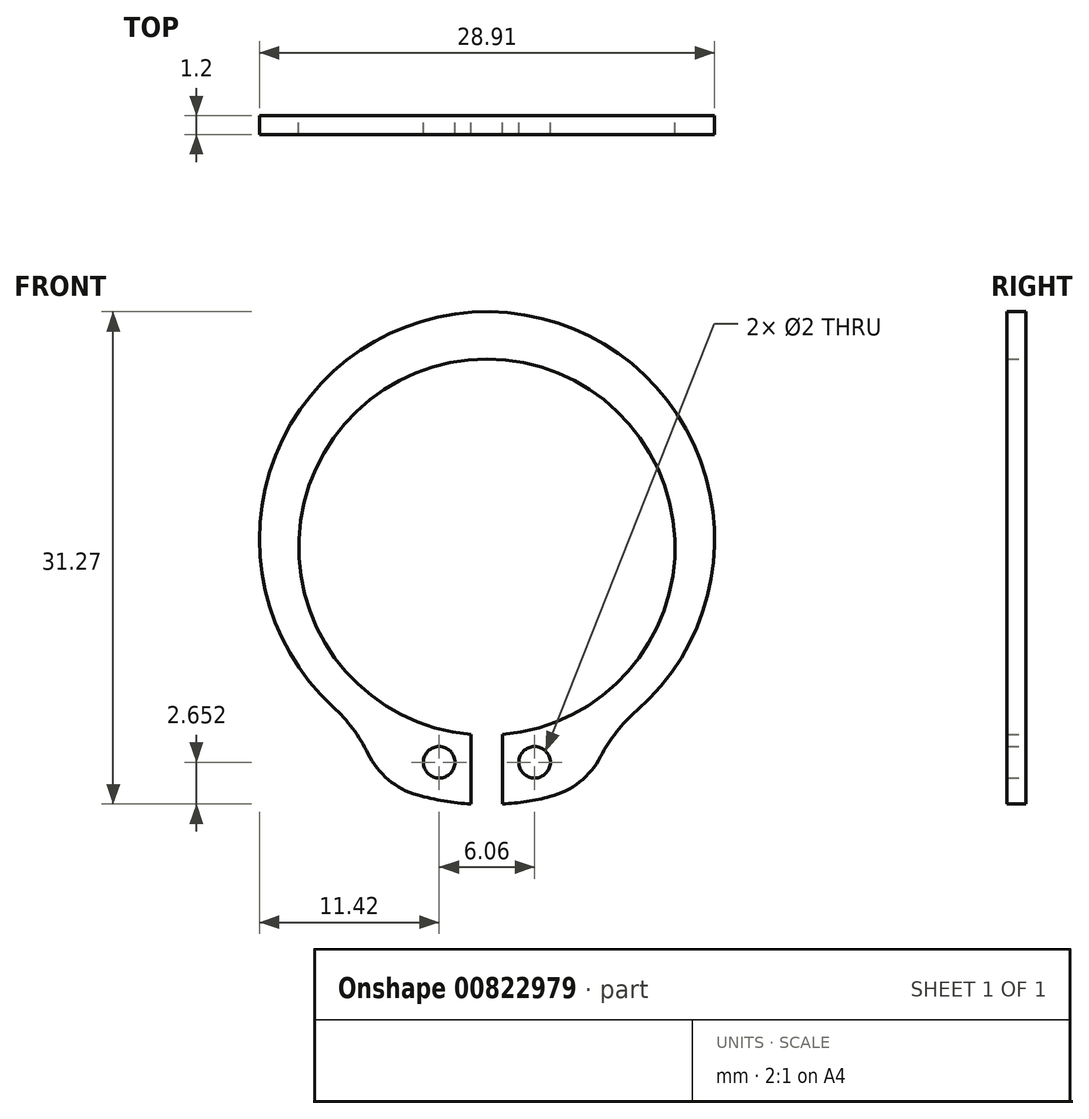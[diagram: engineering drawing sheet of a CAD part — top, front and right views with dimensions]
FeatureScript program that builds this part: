
annotation { "Feature Type Name" : "Feature", "Feature Type Description" : "" }
export const myFeature = defineFeature(function(context is Context, id is Id, definition is map)
    precondition{}
    {
        {
            var Q0;
            Q0=qCreatedBy(makeId("Front.planeOp"),FACE);
            var sketch = newSketch(context, id + "F0", { "sketchPlane" : qUnion([Q0])});
            skArc(sketch, "E0", {"start": v(1, -11.9) * mm, "mid": v(0, 11.95) * mm, "end": v(-1, -11.9) * mm});
            skCircle(sketch, "E1.0", {"center": v(0, 0) * mm, "radius": 14.95 * mm, "construction": true});
            skArc(sketch, "E2.0", {"start": v(1, -16.32) * mm, "mid": v(3.83, -15.9) * mm, "end": v(6.54, -14.99) * mm});
            skLineSegment(sketch, "E3", {"start": v(0, -16.35) * mm, "end": v(0, 16.35) * mm, "construction": true});
            skLineSegment(sketch, "E4.0", {"start": v(1, -16.35) * mm, "end": v(1, -11.9) * mm});
            skLineSegment(sketch, "E5.0", {"start": v(-1, -16.35) * mm, "end": v(-1, -11.9) * mm});
            skCircle(sketch, "E6", {"center": v(3.03, -13.67) * mm, "radius": 1 * mm});
            skLineSegment(sketch, "E7", {"start": v(3.03, -13.67) * mm, "end": v(0, 0) * mm, "construction": true});
            skCircle(sketch, "E8", {"center": v(0, 0) * mm, "radius": 14 * mm, "construction": true});
            skCircle(sketch, "E9.MirrorC", {"center": v(-3.03, -13.67) * mm, "radius": 1 * mm});
            skLineSegment(sketch, "E10", {"start": v(6.54, -14.99) * mm, "end": v(5.54, -12.86) * mm});
            skLineSegment(sketch, "E11.trimOffspring", {"start": v(-5.91, -12.7) * mm, "end": v(-6.9, -14.82) * mm});
            skPoint(sketch, "E12", {"position": v(0, 14.95) * mm});
            skArc(sketch, "E13", {"start": v(5.54, -12.86) * mm, "mid": v(0.22, 14.95) * mm, "end": v(-5.91, -12.7) * mm});
            skArc(sketch, "E14.trimOffspring", {"start": v(-6.9, -14.82) * mm, "mid": v(-4.02, -15.85) * mm, "end": v(-1, -16.32) * mm});
            skArc(sketch, "E15.trimOffspring", {"start": v(0, 16.35) * mm, "mid": v(0, 16.35) * mm, "end": v(0, 16.35) * mm});
            skSolve(sketch);
        }
        {
            var Q0;
            Q0 = qSketchRegion(id + "F0", true);
            extrude(context, id + "F1", {"entities" : qUnion([Q0]), "depth" : 1.2 * mm, "offsetDistance" : 25 * mm});
        }
        {
            var Q0;
            Q0=makeQuery(id+"F1.opExtrude","SWEPT_EDGE",EDGE,{"disambiguationData":[OSD([sQuery(id+"F0.wireOp",EDGE,"E11.trimOffspring"),sQuery(id+"F0.wireOp",EDGE,"E13")])]});
            var Q1;
            Q1=makeQuery(id+"F1.opExtrude","SWEPT_EDGE",EDGE,{"disambiguationData":[OSD([sQuery(id+"F0.wireOp",EDGE,"E10"),sQuery(id+"F0.wireOp",EDGE,"E13")])]});
            fillet(context, id + "F2", {"entities" : qUnion([Q0, Q1]), "radius" : 10 * mm, "tangentPropagation" : true, "allowEdgeOverflow" : false});
        }
        {
            var Q0;
            Q0=makeQuery(id+"F2.opFillet","BLEND_EDGE",EDGE,{"blendedFrom":[makeQuery(id+"F1.opExtrude","SWEPT_EDGE",EDGE,{"disambiguationData":[OSD([sQuery(id+"F0.wireOp",EDGE,"E11.trimOffspring"),sQuery(id+"F0.wireOp",EDGE,"E13")])]}),makeQuery(id+"F1.opExtrude","SWEPT_FACE",FACE,{"disambiguationData":[OSD([sQuery(id+"F0.wireOp",EDGE,"E14.trimOffspring")])]})],"blendedInto":[makeQuery(id+"F1.opExtrude","SWEPT_FACE",FACE,{"disambiguationData":[OSD([sQuery(id+"F0.wireOp",EDGE,"E14.trimOffspring")])]})]});
            var Q1;
            Q1=makeQuery(id+"F2.opFillet","BLEND_EDGE",EDGE,{"blendedFrom":[makeQuery(id+"F1.opExtrude","SWEPT_EDGE",EDGE,{"disambiguationData":[OSD([sQuery(id+"F0.wireOp",EDGE,"E10"),sQuery(id+"F0.wireOp",EDGE,"E13")])]}),makeQuery(id+"F1.opExtrude","SWEPT_FACE",FACE,{"disambiguationData":[OSD([sQuery(id+"F0.wireOp",EDGE,"E2.0")])]})],"blendedInto":[makeQuery(id+"F1.opExtrude","SWEPT_FACE",FACE,{"disambiguationData":[OSD([sQuery(id+"F0.wireOp",EDGE,"E2.0")])]})]});
            fillet(context, id + "F3", {"entities" : qUnion([Q0, Q1]), "radius" : 5 * mm, "tangentPropagation" : true, "allowEdgeOverflow" : false});
        }
    });
